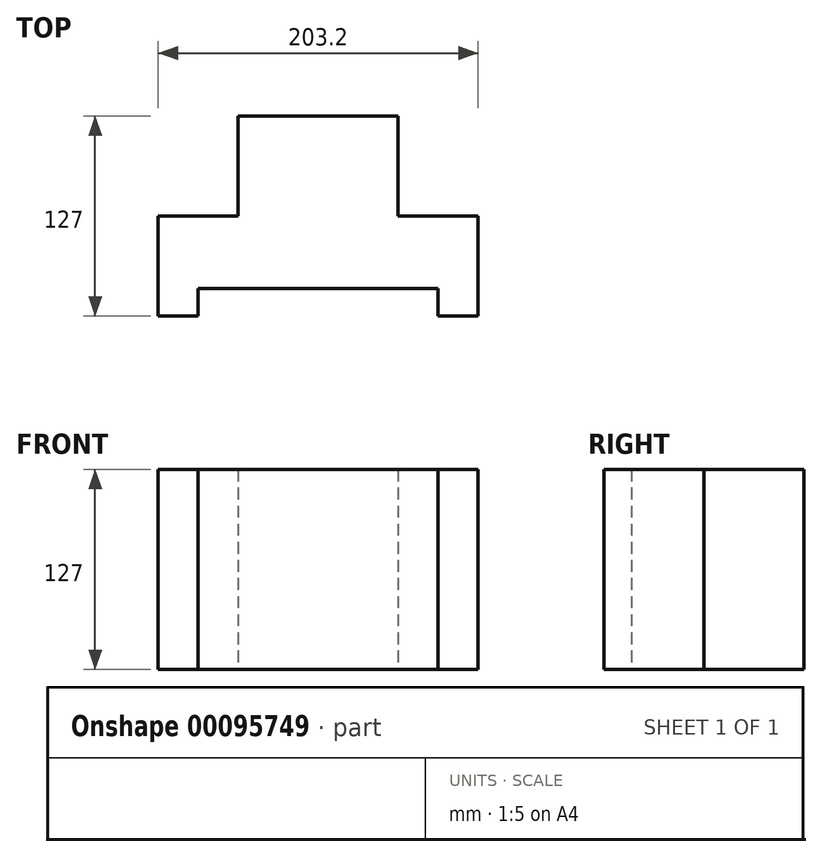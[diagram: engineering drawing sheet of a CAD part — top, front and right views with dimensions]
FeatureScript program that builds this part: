
annotation { "Feature Type Name" : "Feature", "Feature Type Description" : "" }
export const myFeature = defineFeature(function(context is Context, id is Id, definition is map)
    precondition{}
    {
        {
            var Q0;
            Q0=qCreatedBy(makeId("Top.planeOp"),FACE);
            var sketch = newSketch(context, id + "F0", { "sketchPlane" : qUnion([Q0])});
            skLineSegment(sketch, "E0", {"start": v(-106.6, -59.11) * mm, "end": v(-106.6, 4.39) * mm});
            skLineSegment(sketch, "E1", {"start": v(-106.6, 4.39) * mm, "end": v(-55.8, 4.39) * mm});
            skLineSegment(sketch, "E2", {"start": v(-55.8, 4.39) * mm, "end": v(-55.8, 67.89) * mm});
            skLineSegment(sketch, "E3", {"start": v(-55.8, 67.89) * mm, "end": v(45.8, 67.89) * mm});
            skLineSegment(sketch, "E4", {"start": v(45.8, 67.89) * mm, "end": v(45.8, 4.39) * mm});
            skLineSegment(sketch, "E5", {"start": v(45.8, 4.39) * mm, "end": v(96.6, 4.39) * mm});
            skLineSegment(sketch, "E6", {"start": v(96.6, 4.39) * mm, "end": v(96.6, -59.11) * mm});
            skLineSegment(sketch, "E7", {"start": v(-106.6, -59.11) * mm, "end": v(-81.2, -59.11) * mm});
            skLineSegment(sketch, "E8", {"start": v(-81.2, -59.11) * mm, "end": v(-81.2, -41.76) * mm});
            skLineSegment(sketch, "E9", {"start": v(-81.2, -41.76) * mm, "end": v(71.2, -41.76) * mm});
            skLineSegment(sketch, "E10", {"start": v(71.2, -41.76) * mm, "end": v(71.2, -59.11) * mm});
            skLineSegment(sketch, "E11", {"start": v(71.2, -59.11) * mm, "end": v(96.6, -59.11) * mm});
            skSolve(sketch);
        }
        {
            var Q0;
            Q0 = qSketchRegion(id + "F0", true);
            extrude(context, id + "F1", {"entities" : qUnion([Q0]), "depth" : 127 * mm});
        }
    });
